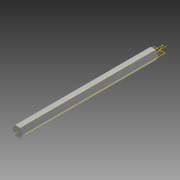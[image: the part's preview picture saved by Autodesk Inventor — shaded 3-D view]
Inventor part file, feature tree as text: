
AUTODESK INVENTOR PART (.ipt)
format: ipt  version: 2014 (Build 180170000, 170)  size: 75,264 bytes
history: native  units: in
note: dims shown in document units (in); Inventor stores cm internally (conversion verified against a paired STEP export)
features: plane x2, extrude x1, other x1, sketch x1
ambient origin geometry x8: Origin, YZ Plane, XZ Plane, XY Plane, X Axis, Y Axis, Z Axis, Center Point
bodies: Solid1 (feature_tree)
feature tree (5):
  extrude  "Extrusion1"  Depth=9.0in TaperAngle=0.0deg
  other  "Work Axis1"
  sketch  "Sketch1"  dims[d0=0.5in d1=9.0in d2=0.0in]
  plane  "Work Plane1"
  plane  "Work Plane2"
